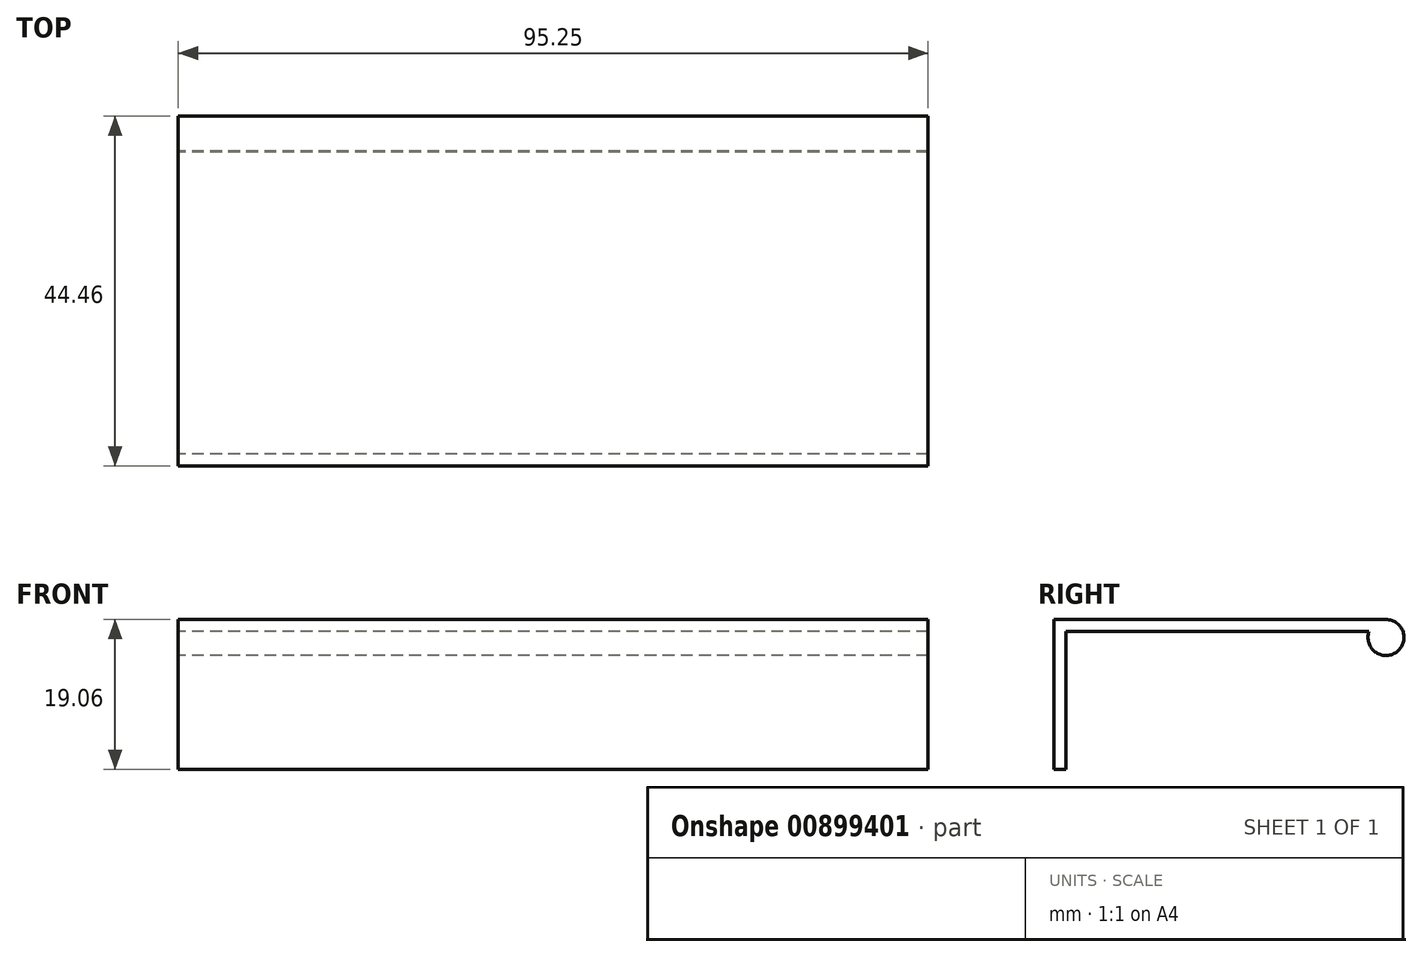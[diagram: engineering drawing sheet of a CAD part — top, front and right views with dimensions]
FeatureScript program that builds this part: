
annotation { "Feature Type Name" : "Feature", "Feature Type Description" : "" }
export const myFeature = defineFeature(function(context is Context, id is Id, definition is map)
    precondition{}
    {
        {
            var Q0;
            Q0=qCreatedBy(makeId("Right.planeOp"),FACE);
            var sketch = newSketch(context, id + "F0", { "sketchPlane" : qUnion([Q0])});
            skLineSegment(sketch, "E0.bottom", {"start": v(22.23, 9.53) * mm, "end": v(-22.23, 9.53) * mm});
            skLineSegment(sketch, "E0.top", {"start": v(22.23, -9.52) * mm, "end": v(-22.23, -9.52) * mm});
            skLineSegment(sketch, "E0.left", {"start": v(22.23, 9.53) * mm, "end": v(22.23, -9.52) * mm});
            skLineSegment(sketch, "E0.right", {"start": v(-22.23, 9.53) * mm, "end": v(-22.23, -9.52) * mm});
            skPoint(sketch, "E0.middle", {"position": v(0, 0) * mm});
            skLineSegment(sketch, "E1", {"start": v(-22.23, -9.52) * mm, "end": v(-20.7, -9.52) * mm});
            skLineSegment(sketch, "E2", {"start": v(-20.7, -9.52) * mm, "end": v(-20.7, 8) * mm});
            skLineSegment(sketch, "E3", {"start": v(-20.7, 8) * mm, "end": v(18.92, 8) * mm});
            skLineSegment(sketch, "E4", {"start": v(22.23, 9.53) * mm, "end": v(22.23, 7.24) * mm});
            skLineSegment(sketch, "E5", {"start": v(22.23, 7.24) * mm, "end": v(19.94, 7.24) * mm});
            skCircle(sketch, "E6", {"center": v(19.94, 7.24) * mm, "radius": 2.29 * mm});
            skSolve(sketch);
        }
        {
            var Q0;
            {var subQ0=sQuery(id+"F0.wireOp",EDGE,"E6");var subQ2=makeQuery(id+"F0.imprint","INTERSECT",VERTEX,{"derivedFrom":[sQuery(id+"F0.wireOp",EDGE,"E0.bottom"),subQ0]});Q0=makeQuery(id+"F0.imprint","IMPRINT",FACE,{"disambiguationData":[TD([[makeQuery(id+"F0.imprint","IMPRINT",EDGE,{"disambiguationData":[TD([[subQ2,-1.0]])],"derivedFrom":subQ0}),1.0]])]});}
            var Q1;
            {var subQ0=sQuery(id+"F0.wireOp",EDGE,"E0.right");Q1=makeQuery(id+"F0.imprint","IMPRINT",FACE,{"disambiguationData":[TD([[makeQuery(id+"F0.imprint","IMPRINT",EDGE,{"derivedFrom":subQ0}),1.0]])]});}
            extrude(context, id + "F1", {"entities" : qUnion([Q0, Q1]), "depth" : 95.25 * mm, "offsetDistance" : 25.4 * mm});
        }
    });
